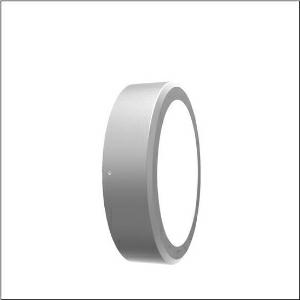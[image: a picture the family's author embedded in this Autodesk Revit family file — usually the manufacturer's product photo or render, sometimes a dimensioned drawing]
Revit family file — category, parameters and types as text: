
# Revit family: cl_31_bulkhead_5cl721603
name_source: partatom
category: Lighting Fixtures
units: mm (PartAtom-declared; Revit-internal decimal feet)

## family parameters
Cut with Voids When Loaded = No
Host = Face
Light Source = No
Part Type = Normal
Room Calculation Point = No
Round Connector Dimension = Use Diameter
Shared = No

## types (1)
- --- (1 x LED, 1570 lm, 14.9 W, 3000K)
    Apparent Load = 15 VA
    CIE Flux Codes = 46 78 95 100 100
    Color Rendering = 80
    Color Temperature = 3000K
    Default Elevation = 1800 mm
    Description = CL 31 Bulkhead, wall and ceiling luminaire, primary light control with reflector, primary optical cover: cover panel, of PC, opal, primary light characteristic: symmetric, installation type: surface-mounted, LED, rated luminous flux: 1.575lm, luminous efficacy: 105lm/W, light colour: 830, colour temperature: 3000K, control gear: ECG DALI, with terminal, 5-pole, max. 2.5mm², mains connection: 220..240V, AC, 50/60Hz, rated input power: 15W, luminaire housing, round, of aluminium, powder-coated, Siteco® metallic grey, diameter: 264mm, height: 63mm, protection rating (complete): IP65, insulation class (complete): insulation class I (protective earthing), certification: CE, ENEC, impact resistance: IK09, permissible operating ambient temperature for outdoor applications: -20..+50°C, packaging unit: 1 piece
    Height = 63 mm
    Lamp = 1 x LED
    Lamp Light Flux = 1570 lm
    Lamp Power = 14.9 W
    Lamp count = 1
    Length = 264 mm
    Luminous efficacy = 105 lm/W
    Manufacturer = Siteco
    ModVariant = No
    Model = 5CL721603
    Mounting Place = Ceiling
    Mounting Type = Surface mounted
    Number of Poles = 1
    OnlyDefault = Yes
    Power Factor = 1
    Product Name = CL 31 Bulkhead
    Product group = wall and ceiling luminaire
    ProductGroupID = 301
    Protection Class = Protection class I
    Protection Degree = IP 65
    RLX_Detail_Level = 1
    RlxData = <blob elided: 36429 chars, md5=f7188bca>
    Socket = socket
    Standby Power = 0 W
    System Light Flux = 1570 lm
    System Power = 15 W
    Type Comments = factory setting: luminous flux: 100 % | dim-lin: 254 | 347 mA
    Type Image = l_1006885.jpg
    URL = http://relux.com
    VarID = @adj_117117
    Voltage = 0 V
    Weight = 0.00 kg
    Width = 0 mm  [stored 0 ft]

note: [stored X ft] marks values corroborated as IEEE doubles in the binary element streams (Revit-internal decimal feet)

## geometry (parser evidence)
native form markers: Blend x4, Sweep x8
no freeform markers — native parametric forms only
